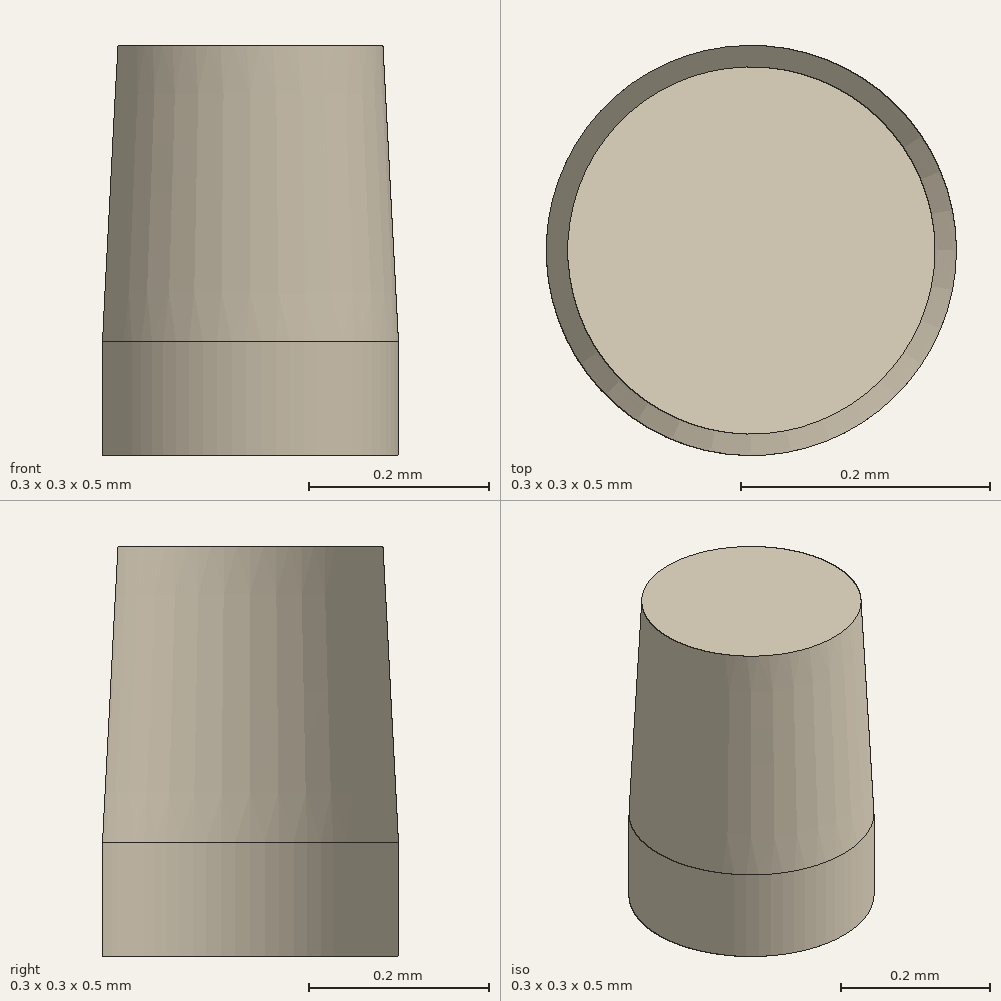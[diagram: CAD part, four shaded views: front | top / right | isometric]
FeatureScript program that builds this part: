
annotation { "Feature Type Name" : "Feature", "Feature Type Description" : "" }
export const myFeature = defineFeature(function(context is Context, id is Id, definition is map)
    precondition{}
    {
        {
            var Q0;
            Q0=qCreatedBy(makeId("Top.planeOp"),FACE);
            var sketch = newSketch(context, id + "F0", { "sketchPlane" : qUnion([Q0])});
            skCircle(sketch, "E0", {"center": v(0, 0) * mm, "radius": 0.17 * mm});
            skSolve(sketch);
        }
        {
            var Q0;
            Q0=makeQuery(id+"F0.imprint","IMPRINT",FACE,{"disambiguationData":[TD([[makeQuery(id+"F0.imprint","IMPRINT",EDGE,{"derivedFrom":sQuery(id+"F0.wireOp",EDGE,"E0")}),1.0]])]});
            extrude(context, id + "F1", {"entities" : qUnion([Q0]), "depth" : 0.13 * mm});
        }
        {
            var Q0;
            Q0=makeQuery(id+"F1.opExtrude","CAP_FACE",FACE,{"disambiguationData":[OSD([sQuery(id+"F0.wireOp",EDGE,"E0")])],"isStart":false});
            extrude(context, id + "F2", {"entities" : qUnion([Q0]), "operationType" : NewBodyOperationType.ADD, "depth" : 0.33 * mm, "hasDraft" : true, "draftAngle" : 3 * degree, "draftPullDirection" : true});
        }
    });
